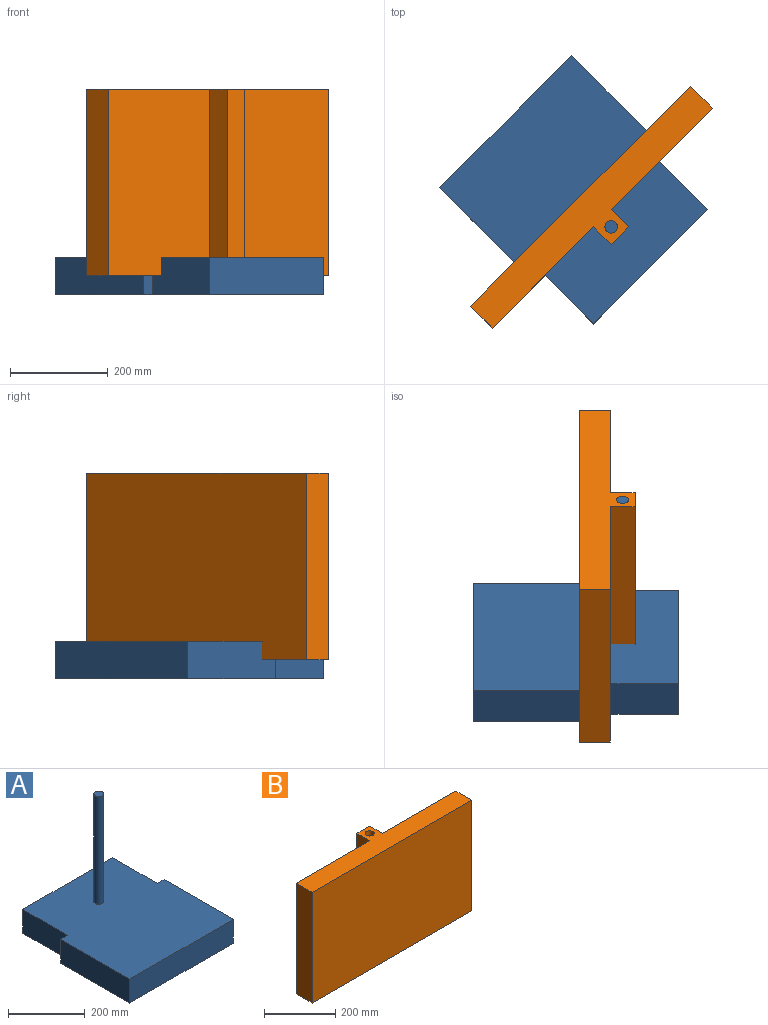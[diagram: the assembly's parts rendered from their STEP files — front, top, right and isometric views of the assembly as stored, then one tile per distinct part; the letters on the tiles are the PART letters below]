
ASSEMBLY  parts=2 mates=1
PART A: 12 faces, bbox 381x419.1x419.1 mm
  f0: plane 165.1x76.2mm, normal (-1,0,0), area 12580.6mm2, adj f1,f7,f8,f9
  f1: plane 76.2x25.4mm, normal (0,1,0), area 1935.5mm2, adj f0,f2,f8,f9
  f2: plane 254x76.2mm, normal (-1,0,0), area 19354.8mm2, adj f1,f3,f8,f9
  f3: plane 381x76.2mm, normal (0,-1,0), area 29032.2mm2, adj f2,f4,f8,f9
  f4: plane 254x76.2mm, normal (1,0,0), area 19354.8mm2, adj f3,f5,f8,f9
  f5: plane 76.2x25.4mm, normal (0,1,0), area 1935.5mm2, adj f4,f6,f8,f9
  f6: plane 165.1x76.2mm, normal (1,0,0), area 12580.6mm2, adj f5,f7,f8,f9
  f7: plane 330.2x76.2mm, normal (0,1,0), area 25161.2mm2, adj f0,f6,f8,f9
  f8: plane 419.1x381mm, normal (0,0,1), area 150783.3mm2, adj f0,f1,f2,f3,f4,f5,f6,f7
  f9: plane 419.1x381mm, normal (0,0,-1), area 151290mm2, adj f0,f1,f2,f3,f4,f5,f6,f7
  f10: cylinder r=12.7mm len=342.9mm, axis (0,0,-1), area 27362.2mm2, adj f8,f11
  f11: plane 25.4x25.4mm, normal (0,0,1), area 506.7mm2, adj f10
PART B: 11 faces, bbox 635x114.3x381 mm
  f0: plane 381x292.1mm, normal (0,1,0), area 111290.1mm2, adj f1,f7,f9,f10
  f1: plane 381x50.8mm, normal (1,0,0), area 19354.8mm2, adj f0,f2,f9,f10
  f2: plane 381x50.8mm, normal (0,1,0), area 19354.8mm2, adj f1,f3,f9,f10
  f3: plane 381x50.8mm, normal (-1,0,0), area 19354.8mm2, adj f2,f4,f9,f10
  f4: plane 381x292.1mm, normal (0,1,0), area 111290.1mm2, adj f3,f5,f9,f10
  f5: plane 381x63.5mm, normal (-1,0,0), area 24193.5mm2, adj f4,f6,f9,f10
  f6: plane 635x381mm, normal (0,-1,0), area 241935mm2, adj f5,f7,f9,f10
  f7: plane 381x63.5mm, normal (1,0,0), area 24193.5mm2, adj f0,f6,f9,f10
  f8: cylinder r=12.7mm len=381mm, axis (0,0,-1), area 30402.4mm2, adj f9,f10
  f9: plane 635x114.3mm, normal (0,0,1), area 42396.4mm2, adj f0,f1,f2,f3,f4,f5,f6,f7
  f10: plane 635x114.3mm, normal (0,0,-1), area 42396.4mm2, adj f0,f1,f2,f3,f4,f5,f6,f7
PLACE A rot(axis=(0,0,-1),135deg) t=(857.33,432.21,-12.1)mm
PLACE B rot(axis=(0,0,-1),135deg) t=(1234.5,773.46,26)mm
MATE revolute A.f10 <-> B.f8  axis (0,0,1) through (1027.96,531,407)mm
